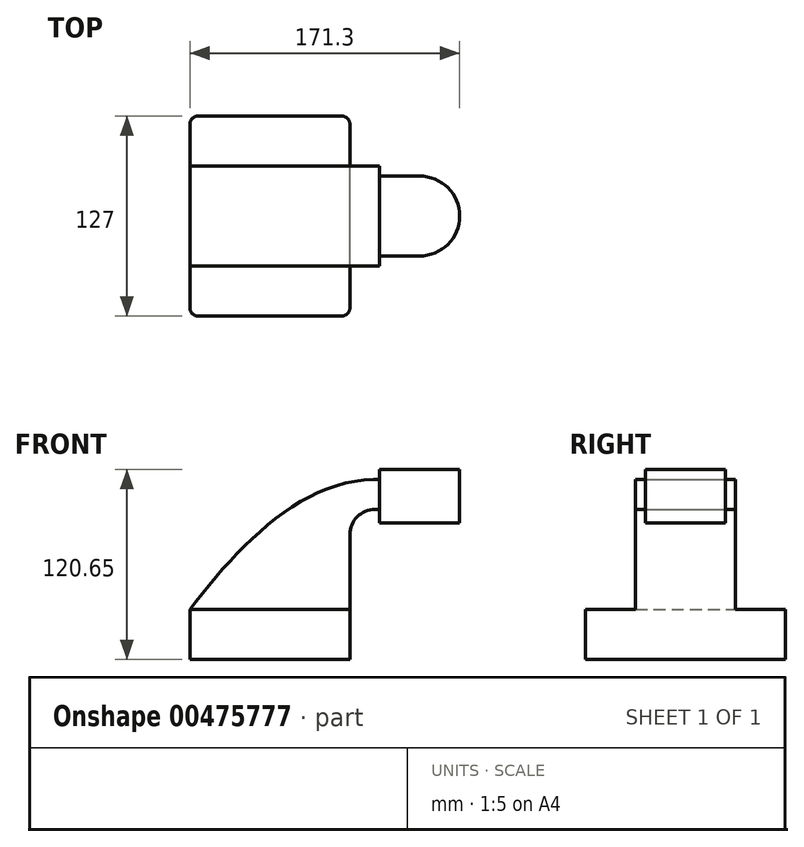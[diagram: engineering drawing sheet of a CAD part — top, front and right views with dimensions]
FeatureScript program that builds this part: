
annotation { "Feature Type Name" : "Feature", "Feature Type Description" : "" }
export const myFeature = defineFeature(function(context is Context, id is Id, definition is map)
    precondition{}
    {
        {
            var Q0;
            Q0=qCreatedBy(makeId("Front.planeOp"),FACE);
            var sketch = newSketch(context, id + "F0", { "sketchPlane" : qUnion([Q0])});
            skLineSegment(sketch, "E0.bottom", {"start": v(50.8, 15.88) * mm, "end": v(-50.8, 15.87) * mm});
            skLineSegment(sketch, "E0.top", {"start": v(50.8, -15.87) * mm, "end": v(-50.8, -15.87) * mm});
            skLineSegment(sketch, "E0.left", {"start": v(50.8, 15.88) * mm, "end": v(50.8, -15.87) * mm});
            skLineSegment(sketch, "E0.right", {"start": v(-50.8, 15.88) * mm, "end": v(-50.8, -15.88) * mm});
            skPoint(sketch, "E0.middle", {"position": v(0, 0) * mm});
            skLineSegment(sketch, "E1.bottom", {"start": v(69.7, 70.81) * mm, "end": v(120.5, 70.81) * mm});
            skLineSegment(sketch, "E1.top", {"start": v(69.7, 104.78) * mm, "end": v(120.5, 104.78) * mm});
            skLineSegment(sketch, "E1.left", {"start": v(69.7, 70.81) * mm, "end": v(69.7, 104.78) * mm});
            skLineSegment(sketch, "E1.right", {"start": v(120.5, 70.81) * mm, "end": v(120.5, 104.78) * mm});
            skPoint(sketch, "E1.middle", {"position": v(95.1, 87.8) * mm});
            skLineSegment(sketch, "E2", {"start": v(50.8, 15.88) * mm, "end": v(50.8, 63.5) * mm});
            skArc(sketch, "E3", {"start": v(50.8, 63.5) * mm, "mid": v(55.45, 74.73) * mm, "end": v(66.67, 79.38) * mm});
            skLineSegment(sketch, "E4", {"start": v(66.67, 79.38) * mm, "end": v(95.1, 79.38) * mm});
            skLineSegment(sketch, "E5.0", {"start": v(66.67, 98.43) * mm, "end": v(94.91, 98.43) * mm});
            skArc(sketch, "E5.1", {"start": v(31.75, 63.5) * mm, "mid": v(41.98, 88.2) * mm, "end": v(66.67, 98.43) * mm});
            skLineSegment(sketch, "E5.2", {"start": v(31.75, 15.88) * mm, "end": v(31.75, 63.5) * mm});
            skLineSegment(sketch, "E6", {"start": v(95.1, 70.81) * mm, "end": v(95.1, 104.78) * mm});
            skFitSpline(sketch, "E7", {"points": [v(-50.8, 15.88) * mm, v(66.67, 98.43) * mm], "startDerivative": vector(90.2, 118.24) * mm, "endDerivative": vector(141.97, 0.86) * mm});
            skSolve(sketch);
        }
        {
            var Q0;
            Q0=makeQuery(id+"F0.imprint","IMPRINT",FACE,{"disambiguationData":[TD([[makeQuery(id+"F0.imprint","IMPRINT",EDGE,{"derivedFrom":sQuery(id+"F0.wireOp",EDGE,"E0.top")}),-1.0]])]});
            extrude(context, id + "F1", {"entities" : qUnion([Q0]), "endBound" : BoundingType.SYMMETRIC, "depth" : 127 * mm});
        }
        {
            var Q0;
            {var subQ3=sQuery(id+"F0.wireOp",EDGE,"E5.2");Q0=makeQuery(id+"F0.imprint","IMPRINT",FACE,{"disambiguationData":[TD([[makeQuery(id+"F0.imprint","IMPRINT",EDGE,{"derivedFrom":subQ3}),1.0]])]});}
            var Q1;
            {var subQ1=sQuery(id+"F0.wireOp",EDGE,"E2");Q1=makeQuery(id+"F0.imprint","IMPRINT",FACE,{"disambiguationData":[TD([[makeQuery(id+"F0.imprint","IMPRINT",EDGE,{"derivedFrom":subQ1}),1.0]])]});}
            extrude(context, id + "F2", {"entities" : qUnion([Q0, Q1]), "operationType" : NewBodyOperationType.ADD, "endBound" : BoundingType.SYMMETRIC, "depth" : 63.5 * mm});
        }
        {
            var Q0;
            {var subQ0=sQuery(id+"F0.wireOp",EDGE,"E1.left");var subQ1=sQuery(id+"F0.wireOp",EDGE,"E1.bottom");var subQ2=makeQuery(id+"F0.imprint","INTERSECT",VERTEX,{"derivedFrom":[subQ1,subQ0]});Q0=makeQuery(id+"F0.imprint","IMPRINT",FACE,{"disambiguationData":[TD([[makeQuery(id+"F0.imprint","IMPRINT",EDGE,{"disambiguationData":[TD([[subQ2,-1.0]])],"derivedFrom":subQ1}),1.0]])]});}
            var Q1;
            {var subQ3=sQuery(id+"F0.wireOp",EDGE,"E1.left");var subQ5=sQuery(id+"F0.wireOp",EDGE,"E1.top");var subQ6=makeQuery(id+"F0.imprint","INTERSECT",VERTEX,{"derivedFrom":[subQ5,subQ3]});Q1=makeQuery(id+"F0.imprint","IMPRINT",FACE,{"disambiguationData":[TD([[makeQuery(id+"F0.imprint","IMPRINT",EDGE,{"disambiguationData":[TD([[subQ6,-1.0]])],"derivedFrom":subQ5}),-1.0]])]});}
            extrude(context, id + "F3", {"entities" : qUnion([Q0, Q1]), "operationType" : NewBodyOperationType.ADD, "endBound" : BoundingType.SYMMETRIC, "depth" : 50.8 * mm});
        }
        {
            var Q0;
            {var subQ0=sQuery(id+"F0.wireOp",EDGE,"E1.right");Q0=makeQuery(id+"F0.imprint","IMPRINT",FACE,{"disambiguationData":[TD([[makeQuery(id+"F0.imprint","IMPRINT",EDGE,{"derivedFrom":subQ0}),1.0]])]});}
            var Q1;
            Q1=sQuery(id+"F0.wireOp",EDGE,"E6");
            revolve(context, id + "F4", {"operationType" : NewBodyOperationType.ADD, "entities" : qUnion([Q0]), "axis" : qUnion([Q1]), "revolveType" : RevolveType.FULL});
        }
        {
            var Q0;
            Q0=makeQuery(id+"F1.opExtrude","CAP_EDGE",EDGE,{"disambiguationData":[OSD([sQuery(id+"F0.wireOp",EDGE,"E0.left")])],"isStart":false});
            var Q1;
            Q1=makeQuery(id+"F1.opExtrude","CAP_EDGE",EDGE,{"disambiguationData":[OSD([sQuery(id+"F0.wireOp",EDGE,"E0.right")])],"isStart":false});
            var Q2;
            Q2=makeQuery(id+"F1.opExtrude","CAP_EDGE",EDGE,{"disambiguationData":[OSD([sQuery(id+"F0.wireOp",EDGE,"E0.right")])],"isStart":true});
            var Q3;
            Q3=makeQuery(id+"F1.opExtrude","CAP_EDGE",EDGE,{"disambiguationData":[OSD([sQuery(id+"F0.wireOp",EDGE,"E0.left")])],"isStart":true});
            fillet(context, id + "F5", {"entities" : qUnion([Q0, Q1, Q2, Q3]), "radius" : 5.08 * mm, "tangentPropagation" : true, "allowEdgeOverflow" : false});
        }
    });
